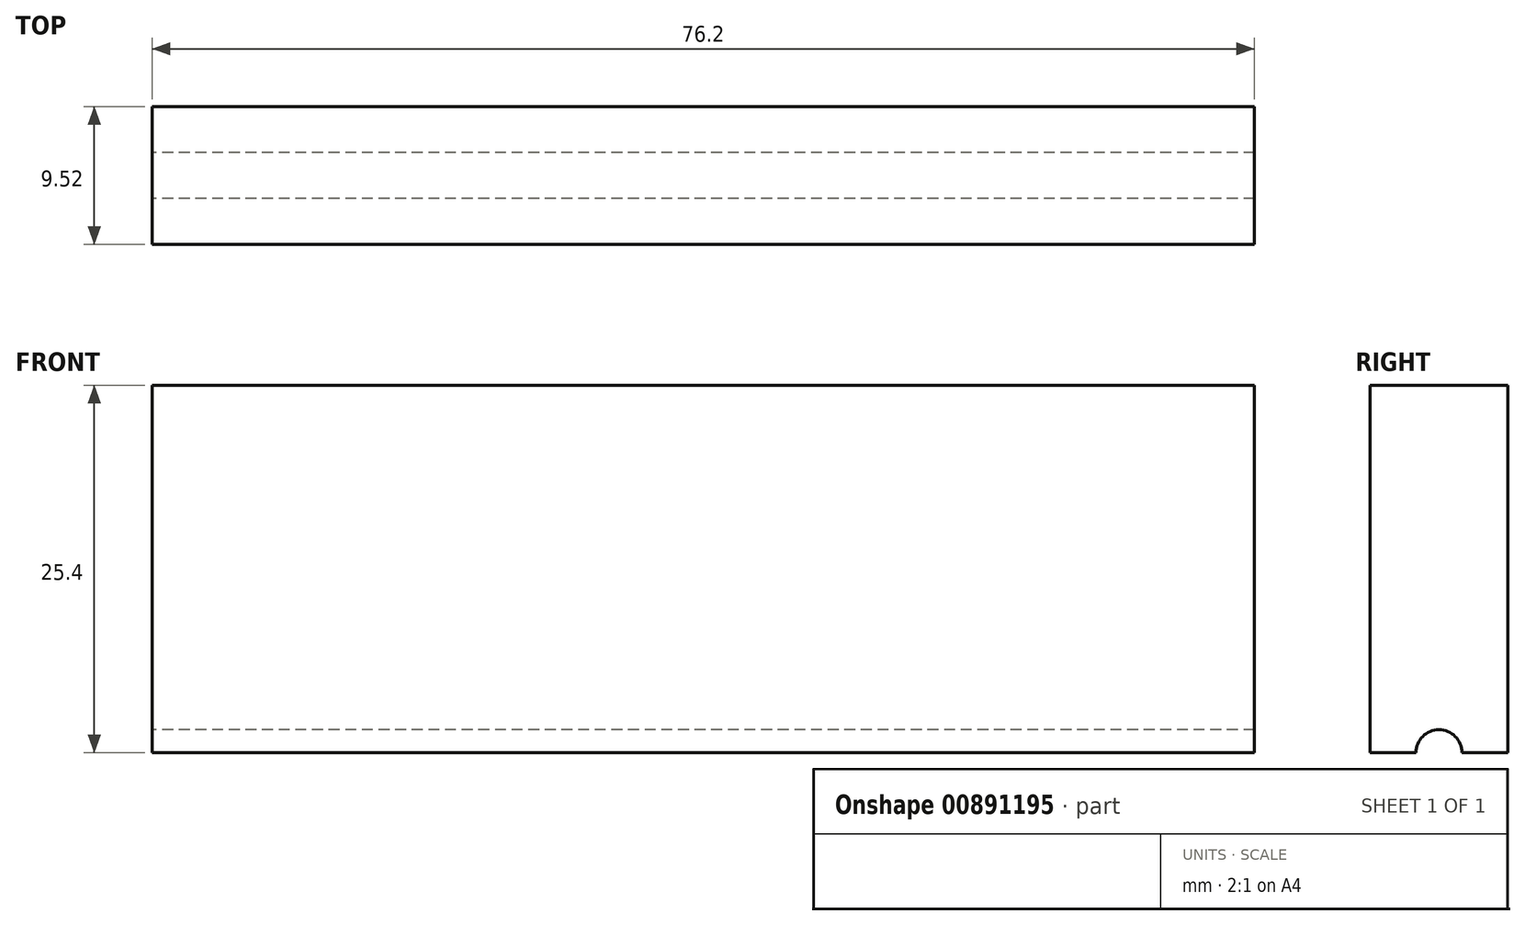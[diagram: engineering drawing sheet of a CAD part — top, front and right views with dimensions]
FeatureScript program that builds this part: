
annotation { "Feature Type Name" : "Feature", "Feature Type Description" : "" }
export const myFeature = defineFeature(function(context is Context, id is Id, definition is map)
    precondition{}
    {
        {
            var Q0;
            Q0=qCreatedBy(makeId("Right.planeOp"),FACE);
            var sketch = newSketch(context, id + "F0", { "sketchPlane" : qUnion([Q0])});
            skLineSegment(sketch, "E0", {"start": v(0, 0) * mm, "end": v(-1.59, 0) * mm, "construction": true});
            skLineSegment(sketch, "E1", {"start": v(-1.59, 0) * mm, "end": v(-4.76, 0) * mm});
            skLineSegment(sketch, "E2", {"start": v(-4.76, 0) * mm, "end": v(-4.76, 25.4) * mm});
            skLineSegment(sketch, "E3", {"start": v(4.76, 25.4) * mm, "end": v(4.76, 0) * mm});
            skLineSegment(sketch, "E4", {"start": v(4.76, 0) * mm, "end": v(1.59, 0) * mm});
            skArc(sketch, "E5", {"start": v(1.59, 0) * mm, "mid": v(0, 1.59) * mm, "end": v(-1.59, 0) * mm});
            skLineSegment(sketch, "E6", {"start": v(4.76, 25.4) * mm, "end": v(-4.76, 25.4) * mm});
            skSolve(sketch);
        }
        {
            var Q0;
            Q0=makeQuery(id+"F0.imprint","IMPRINT",FACE,{"disambiguationData":[TD([[makeQuery(id+"F0.imprint","IMPRINT",EDGE,{"derivedFrom":sQuery(id+"F0.wireOp",EDGE,"E1")}),-1.0]])]});
            extrude(context, id + "F1", {"entities" : qUnion([Q0]), "depth" : 76.2 * mm, "offsetDistance" : 25.4 * mm});
        }
    });
